# Revit family: RSV_14_18_150_10Ø_12Ø_test
name_source: partatom
category: Generic Models
units: mm (PartAtom-declared; Revit-internal decimal feet)

## family parameters
Always vertical = No
Can host rebar = Yes
Cut with Voids When Loaded = No
Part Type = Normal
Room Calculation Point = No
Round Connector Dimension = Use Diameter
Shared = No
Work Plane-Based = Yes

## types (6) — shared parameters
CenterToCenter = 150 mm
Default Elevation = 1219 mm
Manufacturer = Recostal
Model = RSV
Total Length = 1250 mm  [stored 4.10105 ft]
URL = https://www.haucon.fi
Width Box 2 = 155 mm  [stored 0.50853 ft]

## per-type parameters (varying)
| type | Diameter Rebar | Length rebar | Width Box | Width Box 3 | Width Box 4 | Width rebar |
| RSV 18 10Ø 150 | 10 mm  [stored 0.0328084 ft] | 540 mm  [stored 1.77165 ft] | 129 mm  [stored 0.423228 ft] | 98 mm | 145 mm | 126 mm  [stored 0.413386 ft] |
| RSV 18 12Ø 150 | 12 mm  [stored 0.0393701 ft] | 610 mm  [stored 2.00131 ft] | 129 mm  [stored 0.423228 ft] | 98 mm | 145 mm | 126 mm  [stored 0.413386 ft] |
| RSV 14 10Ø 150 | 10 mm  [stored 0.0328084 ft] | 540 mm  [stored 1.77165 ft] | 89 mm  [stored 0.291995 ft] | 58 mm | 105 mm | 86 mm  [stored 0.282152 ft] |
| RSV 14 12Ø 150 | 12 mm  [stored 0.0393701 ft] | 610 mm  [stored 2.00131 ft] | 89 mm  [stored 0.291995 ft] | 58 mm | 105 mm | 86 mm  [stored 0.282152 ft] |
| RSV 18 8Ø 150 | 8 mm  [stored 0.0262467 ft] | 470 mm  [stored 1.54199 ft] | 129 mm  [stored 0.423228 ft] | 98 mm | 145 mm | 126 mm  [stored 0.413386 ft] |
| RSV 14 8Ø 150 | 8 mm  [stored 0.0262467 ft] | 470 mm  [stored 1.54199 ft] | 89 mm  [stored 0.291995 ft] | 58 mm | 105 mm | 86 mm  [stored 0.282152 ft] |

note: [stored X ft] marks values corroborated as IEEE doubles in the binary element streams (Revit-internal decimal feet)

## geometry (parser evidence)
native form markers: Sweep x12
no freeform markers — native parametric forms only
